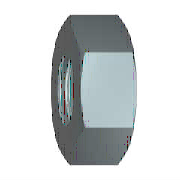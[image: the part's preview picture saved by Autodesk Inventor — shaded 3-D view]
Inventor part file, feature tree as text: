
AUTODESK INVENTOR PART (.ipt)
format: ipt  version: 2023 (Build 270158000, 158)  size: 164,352 bytes
history: native  units: mm (DEFAULTED — no unit token found)
features: sketch x3, other x2, extrude x1, hole x1, plane x1
ambient origin geometry x7: Origin, YZ Plane, XZ Plane, X Axis, Y Axis, Z Axis, Center Point
bodies: Solid1 (feature_tree)
feature tree (8):
  extrude  "Базовый элемент"  Depth=20.78461mm
  other  "Фаска1"
  hole  "Резьба"  [1 undecoded]
  other  "Work Axis1"
  plane  "Work Plane1"
  sketch  "Эскиз1"
  sketch  "Эскиз2"
  sketch  "Эскиз3"
note: 1 required parameter value undecoded (feature->parameter linkage not recoverable at this tier; creation-order binding heuristic only, values carry confidence <= 0.55)
